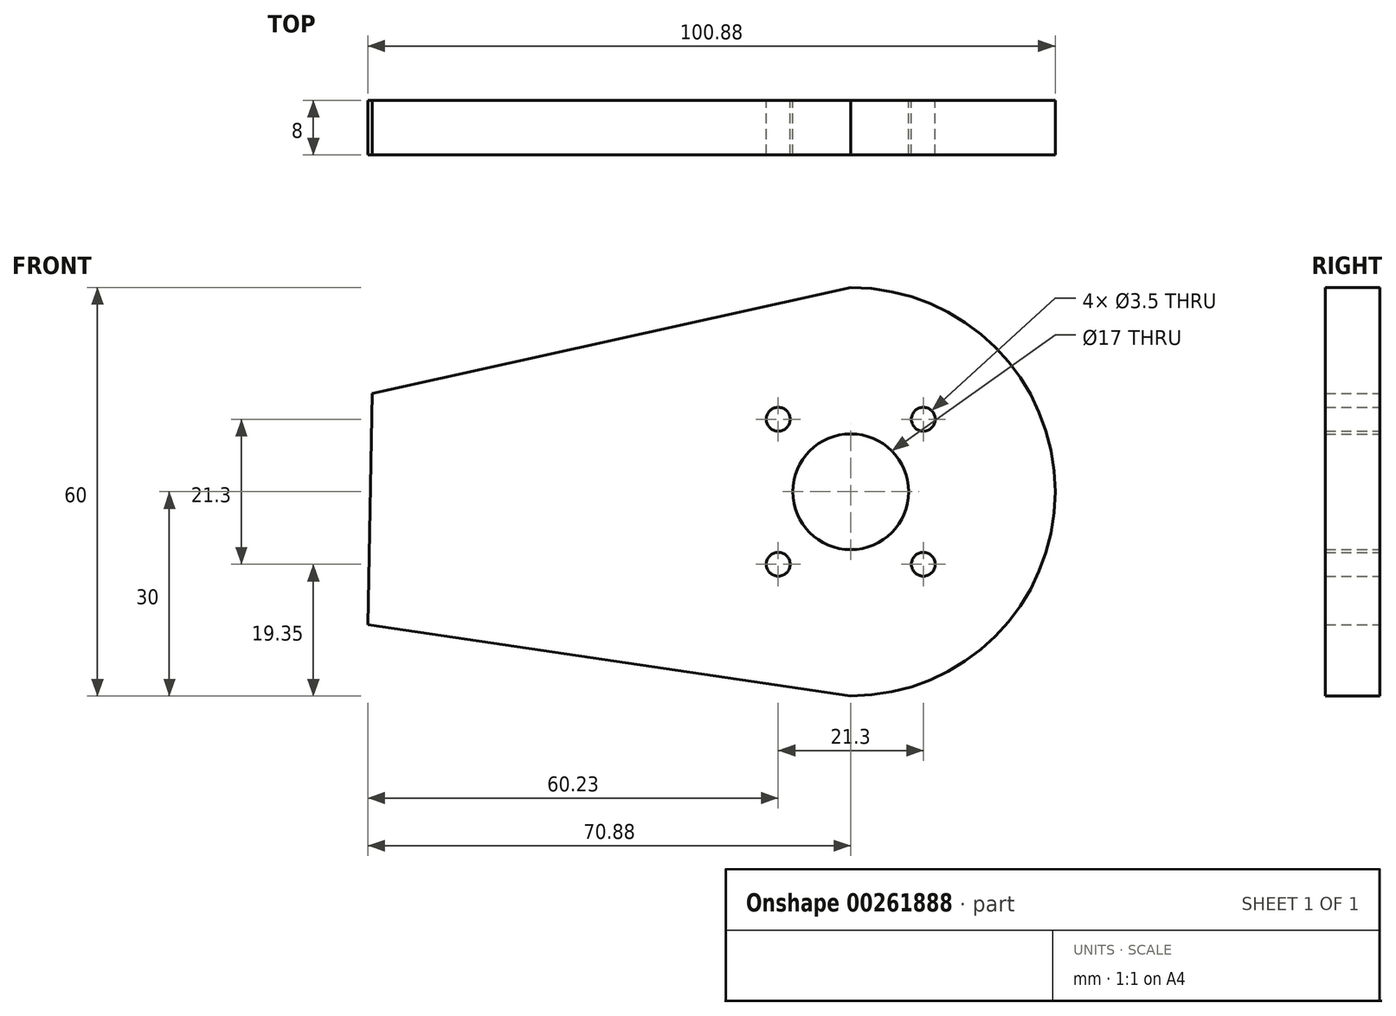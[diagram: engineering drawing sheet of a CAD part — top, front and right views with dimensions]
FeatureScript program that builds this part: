
annotation { "Feature Type Name" : "Feature", "Feature Type Description" : "" }
export const myFeature = defineFeature(function(context is Context, id is Id, definition is map)
    precondition{}
    {
        {
            var Q0;
            Q0=qCreatedBy(makeId("Front.planeOp"),FACE);
            var sketch = newSketch(context, id + "F0", { "sketchPlane" : qUnion([Q0])});
            skArc(sketch, "E0", {"start": v(0, -30) * mm, "mid": v(30, 0) * mm, "end": v(0, 30) * mm});
            skCircle(sketch, "E1", {"center": v(0, 0) * mm, "radius": 8.5 * mm});
            skCircle(sketch, "E2", {"center": v(-10.65, 10.65) * mm, "radius": 1.75 * mm});
            skCircle(sketch, "E3", {"center": v(-10.65, -10.65) * mm, "radius": 1.75 * mm});
            skCircle(sketch, "E4", {"center": v(10.65, -10.65) * mm, "radius": 1.75 * mm});
            skCircle(sketch, "E5", {"center": v(10.65, 10.65) * mm, "radius": 1.75 * mm});
            skLineSegment(sketch, "E6", {"start": v(0, 30) * mm, "end": v(-70.27, 14.44) * mm});
            skLineSegment(sketch, "E7", {"start": v(0, -30) * mm, "end": v(-70.88, -19.56) * mm});
            skLineSegment(sketch, "E8", {"start": v(-70.88, -19.56) * mm, "end": v(-70.27, 14.44) * mm});
            skLineSegment(sketch, "E9", {"start": v(10.65, 10.65) * mm, "end": v(10.65, -10.65) * mm, "construction": true});
            skLineSegment(sketch, "E10", {"start": v(10.65, 10.65) * mm, "end": v(-10.65, 10.65) * mm, "construction": true});
            skLineSegment(sketch, "E11", {"start": v(-10.65, 10.65) * mm, "end": v(-10.65, -10.65) * mm, "construction": true});
            skLineSegment(sketch, "E12", {"start": v(10.65, -10.65) * mm, "end": v(-10.65, -10.65) * mm, "construction": true});
            skSolve(sketch);
        }
        {
            var Q0;
            Q0 = qSketchRegion(id + "F0", true);
            extrude(context, id + "F1", {"entities" : qUnion([Q0]), "depth" : 8 * mm});
        }
    });
